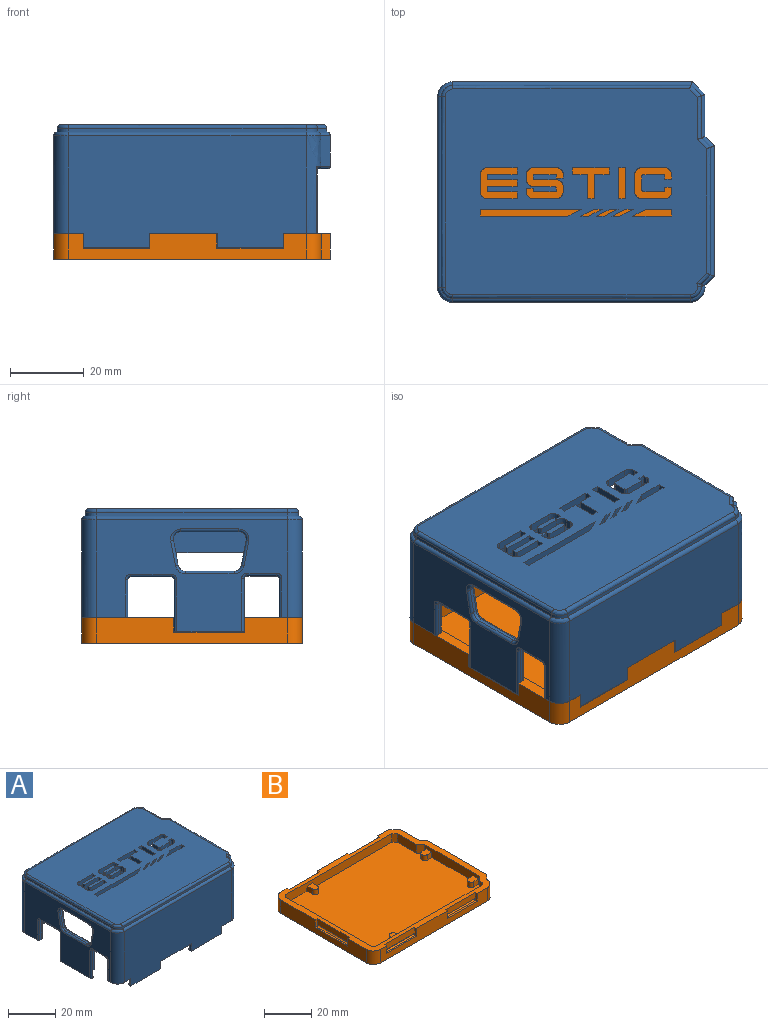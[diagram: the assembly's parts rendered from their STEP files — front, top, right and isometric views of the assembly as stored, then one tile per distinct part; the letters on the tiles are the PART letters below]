
ASSEMBLY  parts=2 mates=1
PART A: 255 faces, bbox 75.3x60.1x54.8 mm
  f0: plane 70.04x54.8mm, normal (0,0,-1), area 3493.9mm2, adj f16,f17,f18,f19,f20,f42,f43,f44
  f1: plane 71.33x56.09mm, normal (0,0,1), area 3615.8mm2, adj f61,f62,f63,f64,f65,f66,f67,f68
  f2: plane 19.01x1.65mm, normal (0,0,-1), area 31.1mm2, adj f43,f74,f79,f99,f129,f150
  f3: plane 17.92x0.8mm, normal (0,0,-1), area 14.3mm2, adj f39,f90,f98,f109
  f4: plane 17.92x0.8mm, normal (0,0,-1), area 14.3mm2, adj f41,f93,f96,f107
  f5: plane 17.92x3.15mm, normal (0,1,0), area 56.4mm2, adj f8,f90,f98,f110
  f6: plane 17.92x3.15mm, normal (0,-1,0), area 56.4mm2, adj f7,f93,f96,f108
  f7: plane 70.52x12.5mm, normal (0,0,-1), area 166.2mm2, adj f6,f10,f36,f37,f40,f41,f43,f44
  f8: plane 71.46x6.25mm, normal (0,0,-1), area 147.3mm2, adj f5,f9,f10,f11,f35,f38,f39,f42
  f9: plane 17.92x3.15mm, normal (0,1,0), area 56.4mm2, adj f8,f89,f97,f103
  f10: plane 51.81x30.35mm, normal (-1,0,0), area 907.2mm2, adj f7,f8,f25,f37,f38,f100,f119,f120
  f11: bspline ~27.5x4.44mm, area 110mm2, adj f8,f12,f28,f39,f156,f158
  f12: plane 8.25x2.54mm, normal (0.71,-0.71,0), area 29.6mm2, adj f11,f13,f29,f157
  f13: plane 35.43x8.25mm, normal (1,0,0), area 292.3mm2, adj f12,f14,f30,f155
  f14: plane 8.25x2.54mm, normal (0.71,0.71,0), area 29.6mm2, adj f13,f15,f31,f154
  f15: plane 11.43x8.25mm, normal (1,0,0), area 94.3mm2, adj f14,f32,f40,f153
  f16: plane 9.5x1.96mm, normal (-0.71,-0.71,0), area 26.4mm2, adj f0,f17,f44,f73
  f17: plane 11.43x9.5mm, normal (-1,0,0), area 108.5mm2, adj f0,f16,f18,f73
  f18: plane 9.5x2.54mm, normal (-0.71,-0.71,0), area 34.1mm2, adj f0,f17,f19,f73
  f19: plane 33.35x9.5mm, normal (-1,0,0), area 316.9mm2, adj f0,f18,f20,f73
  f20: plane 9.5x2.54mm, normal (-0.71,0.71,0), area 34.1mm2, adj f0,f19,f21,f59,f73
  f21: bspline ~50x2.98mm, area 29.3mm2, adj f20,f42,f59,f73
  f22: bspline ~2.41x1.59mm, area 0mm2, adj f24,f25,f53
  f23: bspline ~1.07x0.98mm, area 0.4mm2, adj f28,f29,f45
  f24: bspline ~4.08x4.06mm, area 8.8mm2, adj f22,f34,f37,f52
  f25: cylinder r=1mm len=51.81mm, axis (0,-1,0), area 81.4mm2, adj f10,f22,f26,f54
  f26: bspline ~4.05x4mm, area 8.8mm2, adj f25,f27,f38,f55
  f27: cylinder r=1mm len=64.54mm, axis (1,0,0), area 101.4mm2, adj f26,f28,f39,f56
  f28: bspline ~4.44x4.03mm, area 9.5mm2, adj f11,f23,f27,f29,f57
  f29: cylinder r=1mm len=3.61mm, axis (0.71,0.71,0), area 5.7mm2, adj f12,f23,f28,f30,f46
  f30: cylinder r=1mm len=35.43mm, axis (0,1,0), area 55mm2, adj f13,f29,f31,f47
  f31: cylinder r=1mm len=3.54mm, axis (-0.71,0.71,0), area 5.6mm2, adj f14,f30,f32,f48
  f32: cylinder r=1mm len=11.84mm, axis (0,1,0), area 17.9mm2, adj f15,f31,f33,f49
  f33: cylinder r=1mm len=4.13mm, axis (-0.71,0.71,0), area 7mm2, adj f32,f34,f40,f50
  f34: cylinder r=1mm len=65.09mm, axis (-1,0,0), area 102mm2, adj f24,f33,f41,f51
  f35: bspline ~50x1.68mm, area 65.6mm2, adj f8,f42,f43,f60
  f36: bspline ~50x1.72mm, area 66mm2, adj f7,f43,f44,f58
  f37: bspline ~27.5x4.02mm, area 163.9mm2, adj f7,f10,f24,f41
  f38: bspline ~27.5x3.98mm, area 163.3mm2, adj f8,f10,f26,f39
  f39: plane 64.54x30.35mm, normal (0,-1,0), area 1848.4mm2, adj f3,f8,f11,f27,f38,f88,f89,f90
  f40: plane 26.5x3.43mm, normal (0.71,0.71,0), area 71.5mm2, adj f7,f15,f33,f41,f151,f152
  f41: plane 65.09x30.35mm, normal (0,1,0), area 1862.9mm2, adj f4,f7,f34,f37,f40,f92,f93,f94
  f42: plane 66.52x27mm, normal (0,1,0), area 1773.4mm2, adj f0,f8,f21,f35,f59,f60,f73,f156
  f43: plane 51.41x27mm, normal (1,0,0), area 855mm2, adj f0,f2,f7,f8,f35,f36,f58,f60
  f44: plane 65.58x27mm, normal (0,-1,0), area 1754.1mm2, adj f0,f7,f16,f36,f58,f73,f151
  f45: extruded ~1x0.43mm, area 0.4mm2, adj f23,f46,f57,f68
  f46: plane 2.61x2.61mm, normal (0.71,-0.71,0), area 3.7mm2, adj f29,f45,f47,f67
  f47: plane 34.6x1mm, normal (1,0,0), area 34.6mm2, adj f30,f46,f48,f65
  f48: plane 2.54x2.54mm, normal (0.71,0.71,0), area 3.6mm2, adj f31,f47,f49,f63
  f49: plane 11.43x1mm, normal (1,0,0), area 11.4mm2, adj f32,f48,f50,f61
  f50: plane 2.84x2.84mm, normal (0.71,0.71,0), area 4mm2, adj f33,f49,f51,f62
  f51: plane 64.64x1mm, normal (0,1,0), area 64.6mm2, adj f34,f50,f52,f64
  f52: extruded ~3.02x3.01mm, area 4.7mm2, adj f24,f51,f53,f66
  f53: plane 1x0mm, normal (-1,0,0), area 0mm2, adj f22,f52,f54
  f54: plane 51.79x1mm, normal (-1,0,0), area 51.8mm2, adj f25,f53,f55,f69
  f55: extruded ~2.99x2.99mm, area 4.6mm2, adj f26,f54,f56,f71
  f56: plane 64.51x1mm, normal (0,-1,0), area 64.5mm2, adj f27,f55,f57,f72
  f57: extruded ~3.35x3.01mm, area 5mm2, adj f28,f45,f56,f70
  f58: extruded ~2x1.71mm, area 5.3mm2, adj f0,f36,f43,f44
  f59: extruded ~2.98x2mm, area 7.8mm2, adj f0,f20,f21,f42
  f60: extruded ~2x1.68mm, area 5.3mm2, adj f0,f35,f42,f43
  f61: bspline ~12.63x1mm, area 18.5mm2, adj f1,f49,f62,f63
  f62: bspline ~3.55x3.55mm, area 5.9mm2, adj f1,f50,f61,f64
  f63: bspline ~3.82x3.82mm, area 5.8mm2, adj f1,f48,f61,f65
  f64: bspline ~67.87x1mm, area 104.5mm2, adj f1,f51,f62,f66
  f65: bspline ~38.06x1mm, area 55.5mm2, adj f1,f47,f63,f67
  f66: bspline ~3.11x3.03mm, area 6.8mm2, adj f1,f52,f64,f69
  f67: bspline ~3.72x3.72mm, area 6.1mm2, adj f1,f46,f65,f68
  f68: bspline ~1.19x1.08mm, area 1.1mm2, adj f1,f45,f67,f70
  f69: bspline ~51.79x1mm, area 84mm2, adj f1,f54,f66,f71
  f70: bspline ~3.35x3.14mm, area 7.2mm2, adj f1,f57,f68,f72
  f71: bspline ~3.02x3.02mm, area 6.6mm2, adj f1,f55,f69,f72
  f72: bspline ~64.51x1mm, area 104.7mm2, adj f1,f56,f70,f71
  f73: plane 55.28x6.34mm, normal (0,0,-1), area 101.2mm2, adj f16,f17,f18,f19,f20,f21,f42,f44
  f74: plane 14.1x1mm, normal (0,1,0), area 10.9mm2, adj f2,f99,f100,f101,f102,f144,f148,f150
  f75: plane 11.05x1mm, normal (0,0,-1), area 11.1mm2, adj f142,f143,f147,f148
  f76: plane 10.25x1mm, normal (0,-1,0), area 10.3mm2, adj f7,f139,f141,f142
  f77: plane 10.5x1mm, normal (0,1,0), area 10.5mm2, adj f8,f132,f136,f138
  f78: plane 8x1mm, normal (0,0,-1), area 8mm2, adj f130,f131,f135,f136
  f79: plane 14.35x1mm, normal (0,-1,0), area 11.2mm2, adj f2,f99,f100,f101,f102,f127,f129,f130
  f80: plane 6.7x1.29mm, normal (0,0.98,0.19), area 6.8mm2, adj f81,f85,f118,f126
  f81: cylinder r=2mm len=2.38mm, axis (-1,0,0), area 3.5mm2, adj f80,f82,f116,f125
  f82: plane 15.77x1mm, normal (0,0,-1), area 15.8mm2, adj f81,f83,f114,f123
  f83: cylinder r=2mm len=2.38mm, axis (-1,0,0), area 3.5mm2, adj f82,f84,f112,f121
  f84: plane 6.7x1.29mm, normal (0,-0.98,0.19), area 6.8mm2, adj f83,f86,f111,f119
  f85: cylinder r=2mm len=1.96mm, axis (-1,0,0), area 2.8mm2, adj f80,f87,f117,f124
  f86: cylinder r=2mm len=1.96mm, axis (-1,0,0), area 2.8mm2, adj f84,f87,f113,f120
  f87: plane 13.19x1mm, normal (0,0,1), area 13.2mm2, adj f85,f86,f115,f122
  f88: plane 17.92x0.8mm, normal (0,0,-1), area 14.3mm2, adj f39,f89,f97,f104
  f89: plane 3.85x1.49mm, normal (1,0,0), area 4.1mm2, adj f8,f9,f39,f88,f103,f104
  f90: plane 3.85x1.49mm, normal (-1,0,0), area 4.1mm2, adj f3,f5,f8,f39,f109,f110
  f91: plane 17.92x3.15mm, normal (0,-1,0), area 56.4mm2, adj f7,f94,f95,f105
  f92: plane 17.92x0.8mm, normal (0,0,-1), area 14.3mm2, adj f41,f94,f95,f106
  f93: plane 3.85x1.48mm, normal (-1,0,0), area 3.6mm2, adj f4,f6,f7,f41,f107,f108
  f94: plane 3.85x1.49mm, normal (1,0,0), area 3.6mm2, adj f7,f41,f91,f92,f105,f106
  f95: plane 3.85x1.48mm, normal (-1,0,0), area 3.6mm2, adj f7,f41,f91,f92,f105,f106
  f96: plane 3.85x1.48mm, normal (1,0,0), area 3.6mm2, adj f4,f6,f7,f41,f107,f108
  f97: plane 3.85x1.49mm, normal (-1,0,0), area 4.1mm2, adj f8,f9,f39,f88,f103,f104
  f98: plane 3.85x1.49mm, normal (1,0,0), area 4.1mm2, adj f3,f5,f8,f39,f109,f110
  f99: plane 19.01x3.15mm, normal (1,0,0), area 59.9mm2, adj f2,f74,f79,f101
  f100: plane 19.01x0.8mm, normal (0,0,-1), area 15mm2, adj f10,f74,f79,f102,f127,f144
  f101: bspline ~20.91x0.7mm, area 13.8mm2, adj f74,f79,f99,f102
  f102: bspline ~20.91x0.7mm, area 14.7mm2, adj f74,f79,f100,f101
  f103: bspline ~19.71x0.67mm, area 10.4mm2, adj f9,f89,f97,f104
  f104: bspline ~19.71x0.7mm, area 13.9mm2, adj f88,f89,f97,f103
  f105: bspline ~19.71x0.7mm, area 13mm2, adj f91,f94,f95,f106
  f106: bspline ~19.71x0.7mm, area 13.9mm2, adj f92,f94,f95,f105
  f107: bspline ~19.71x0.7mm, area 13.9mm2, adj f4,f93,f96,f108
  f108: bspline ~19.71x0.7mm, area 13mm2, adj f6,f93,f96,f107
  f109: bspline ~19.71x0.7mm, area 13.9mm2, adj f3,f90,f98,f110
  f110: bspline ~19.71x0.67mm, area 10.4mm2, adj f5,f90,f98,f109
  f111: cylinder r=0.75mm len=6.84mm, axis (0,0.19,0.98), area 8mm2, adj f43,f84,f112,f113
  f112: torus R=2.75mm, axis (-1,0,0), area 4.7mm2, adj f43,f83,f111,f114
  f113: torus R=2.75mm, axis (-1,0,0), area 3.7mm2, adj f43,f86,f111,f115
  f114: cylinder r=0.75mm len=15.77mm, axis (0,-1,0), area 18.6mm2, adj f43,f82,f112,f116
  f115: cylinder r=0.75mm len=13.19mm, axis (0,1,0), area 15.5mm2, adj f43,f87,f113,f117
  f116: torus R=2.75mm, axis (-1,0,0), area 4.7mm2, adj f43,f81,f114,f118
  f117: torus R=2.75mm, axis (-1,0,0), area 3.7mm2, adj f43,f85,f115,f118
  f118: cylinder r=0.75mm len=6.84mm, axis (0,0.19,-0.98), area 8mm2, adj f43,f80,f116,f117
  f119: cylinder r=0.75mm len=6.84mm, axis (0,0.19,0.98), area 8mm2, adj f10,f84,f120,f121
  f120: torus R=2.75mm, axis (-1,0,0), area 3.7mm2, adj f10,f86,f119,f122
  f121: torus R=2.75mm, axis (-1,0,0), area 4.7mm2, adj f10,f83,f119,f123
  f122: cylinder r=0.75mm len=13.19mm, axis (0,1,0), area 15.5mm2, adj f10,f87,f120,f124
  f123: cylinder r=0.75mm len=15.77mm, axis (0,-1,0), area 18.6mm2, adj f10,f82,f121,f125
  f124: torus R=2.75mm, axis (-1,0,0), area 3.7mm2, adj f10,f85,f122,f126
  f125: torus R=2.75mm, axis (-1,0,0), area 4.7mm2, adj f10,f81,f123,f126
  f126: cylinder r=0.75mm len=6.84mm, axis (0,0.19,-0.98), area 8mm2, adj f10,f80,f124,f125
  f127: cylinder r=0.75mm len=14.35mm, axis (0,0,1), area 16.9mm2, adj f10,f79,f100,f128
  f128: torus R=1.5mm, axis (-1,0,0), area 1.9mm2, adj f10,f127,f130,f131
  f129: cylinder r=0.75mm len=10.5mm, axis (0,0,1), area 12.4mm2, adj f2,f43,f79,f133
  f130: cylinder r=0.75mm len=1mm, axis (1,0,0), area 1.2mm2, adj f78,f79,f128,f133
  f131: cylinder r=0.75mm len=8mm, axis (0,-1,0), area 9.4mm2, adj f10,f78,f128,f134
  f132: cylinder r=0.75mm len=10.5mm, axis (0,0,-1), area 12.4mm2, adj f8,f10,f77,f134
  f133: torus R=1.5mm, axis (-1,0,0), area 1.9mm2, adj f43,f129,f130,f135
  f134: torus R=1.5mm, axis (-1,0,0), area 1.9mm2, adj f10,f131,f132,f136
  f135: cylinder r=0.75mm len=8mm, axis (0,-1,0), area 9.4mm2, adj f43,f78,f133,f137
  f136: cylinder r=0.75mm len=1mm, axis (1,0,0), area 1.2mm2, adj f77,f78,f134,f137
  f137: torus R=1.5mm, axis (-1,0,0), area 1.9mm2, adj f43,f135,f136,f138
  f138: cylinder r=0.75mm len=10.5mm, axis (0,0,-1), area 12.4mm2, adj f8,f43,f77,f137
  f139: cylinder r=0.75mm len=10.25mm, axis (0,0,1), area 12.1mm2, adj f7,f10,f76,f140
  f140: torus R=1.5mm, axis (-1,0,0), area 1.9mm2, adj f10,f139,f142,f143
  f141: cylinder r=0.75mm len=10.25mm, axis (0,0,1), area 12.1mm2, adj f7,f43,f76,f145
  f142: cylinder r=0.75mm len=1mm, axis (1,0,0), area 1.2mm2, adj f75,f76,f140,f145
  f143: cylinder r=0.75mm len=11.05mm, axis (0,-1,0), area 13mm2, adj f10,f75,f140,f146
  f144: cylinder r=0.75mm len=14.1mm, axis (0,0,-1), area 16.6mm2, adj f10,f74,f100,f146
  f145: torus R=1.5mm, axis (-1,0,0), area 1.9mm2, adj f43,f141,f142,f147
  f146: torus R=1.5mm, axis (-1,0,0), area 1.9mm2, adj f10,f143,f144,f148
  f147: cylinder r=0.75mm len=11.05mm, axis (0,-1,0), area 13mm2, adj f43,f75,f145,f149
  f148: cylinder r=0.75mm len=1mm, axis (1,0,0), area 1.2mm2, adj f74,f75,f146,f149
  f149: torus R=1.5mm, axis (-1,0,0), area 1.9mm2, adj f43,f147,f148,f150
  f150: cylinder r=0.75mm len=10.25mm, axis (0,0,-1), area 12.1mm2, adj f2,f43,f74,f149
  f151: cylinder r=0.75mm len=18.25mm, axis (0,0,-1), area 31.4mm2, adj f7,f40,f44,f73,f152
  f152: cylinder r=0.75mm len=2.74mm, axis (-0.71,0.71,0), area 3.1mm2, adj f40,f73,f151,f153
  f153: cylinder r=0.75mm len=11.74mm, axis (0,1,0), area 13.5mm2, adj f15,f73,f152,f154
  f154: cylinder r=0.75mm len=3.29mm, axis (-0.71,0.71,0), area 4.2mm2, adj f14,f73,f153,f155
  f155: cylinder r=0.75mm len=35.43mm, axis (0,1,0), area 41.4mm2, adj f13,f73,f154,f157
  f156: cylinder r=0.75mm len=18.25mm, axis (0,0,1), area 31.6mm2, adj f8,f11,f42,f73,f158
  f157: cylinder r=0.75mm len=3.32mm, axis (0.71,0.71,0), area 4.3mm2, adj f12,f73,f155,f158
  f158: bspline ~4.3x2.3mm, area 3.7mm2, adj f11,f73,f156,f157
  f159: plane 8.13x2.5mm, normal (0,-1,0), area 20.3mm2, adj f0,f1,f160,f174
  f160: extruded ~2.5x1.88mm, area 7.4mm2, adj f0,f1,f159,f161
  f161: plane 4.69x2.5mm, normal (1,0,0), area 11.7mm2, adj f0,f1,f160,f162
  f162: extruded ~2.5x1.88mm, area 7.4mm2, adj f0,f1,f161,f163
  f163: plane 8.13x2.5mm, normal (0,1,0), area 20.3mm2, adj f0,f1,f162,f164
  f164: plane 2.5x1.88mm, normal (-1,0,0), area 4.7mm2, adj f0,f1,f163,f165
  f165: plane 7.81x2.5mm, normal (0,-1,0), area 19.5mm2, adj f0,f1,f164,f166
  f166: extruded ~2.5x0.31mm, area 1.2mm2, adj f0,f1,f165,f167
  f167: plane 2.5x1.09mm, normal (-1,0,0), area 2.7mm2, adj f0,f1,f166,f168
  f168: plane 8.13x2.5mm, normal (0,1,0), area 20.3mm2, adj f0,f1,f167,f169
  f169: plane 2.5x1.88mm, normal (-1,0,0), area 4.7mm2, adj f0,f1,f168,f170
  f170: plane 8.13x2.5mm, normal (0,-1,0), area 20.3mm2, adj f0,f1,f169,f171
  f171: plane 2.5x1.09mm, normal (-1,0,0), area 2.7mm2, adj f0,f1,f170,f172
  f172: extruded ~2.5x0.31mm, area 1.2mm2, adj f0,f1,f171,f173
  f173: plane 7.81x2.5mm, normal (0,1,0), area 19.5mm2, adj f0,f1,f172,f174
  f174: plane 2.5x1.88mm, normal (-1,0,0), area 4.7mm2, adj f0,f1,f159,f173
  f175: plane 6.8x2.5mm, normal (0,-1,0), area 17mm2, adj f0,f1,f176,f178
  f176: plane 3.75x2.5mm, normal (0.45,-0.89,0), area 10.5mm2, adj f0,f1,f175,f177
  f177: plane 10.55x2.5mm, normal (0,1,0), area 26.4mm2, adj f0,f1,f176,f178
  f178: plane 2.5x1.88mm, normal (-1,0,0), area 4.7mm2, adj f0,f1,f175,f177
  f179: plane 2.5x2.13mm, normal (0,-1,0), area 5.3mm2, adj f0,f1,f180,f182
  f180: plane 3.75x2.5mm, normal (0.45,-0.89,0), area 10.5mm2, adj f0,f1,f179,f181
  f181: plane 2.5x2.13mm, normal (0,1,0), area 5.3mm2, adj f0,f1,f180,f182
  f182: plane 3.75x2.5mm, normal (-0.45,0.89,0), area 10.5mm2, adj f0,f1,f179,f181
  f183: plane 27.51x2.5mm, normal (0,-1,0), area 68.8mm2, adj f0,f1,f184,f186
  f184: plane 2.5x1.88mm, normal (1,0,0), area 4.7mm2, adj f0,f1,f183,f185
  f185: plane 23.76x2.5mm, normal (0,1,0), area 59.4mm2, adj f0,f1,f184,f186
  f186: plane 3.75x2.5mm, normal (-0.45,0.89,0), area 10.5mm2, adj f0,f1,f183,f185
  f187: plane 2.5x2.13mm, normal (0,-1,0), area 5.3mm2, adj f0,f1,f188,f190
  f188: plane 3.75x2.5mm, normal (0.45,-0.89,0), area 10.5mm2, adj f0,f1,f187,f189
  f189: plane 2.5x2.13mm, normal (0,1,0), area 5.3mm2, adj f0,f1,f188,f190
  f190: plane 3.75x2.5mm, normal (-0.45,0.89,0), area 10.5mm2, adj f0,f1,f187,f189
  f191: plane 2.5x2.13mm, normal (0,-1,0), area 5.3mm2, adj f0,f1,f192,f194
  f192: plane 3.75x2.5mm, normal (0.45,-0.89,0), area 10.5mm2, adj f0,f1,f191,f193
  f193: plane 2.5x2.13mm, normal (0,1,0), area 5.3mm2, adj f0,f1,f192,f194
  f194: plane 3.75x2.5mm, normal (-0.45,0.89,0), area 10.5mm2, adj f0,f1,f191,f193
  f195: extruded ~2.5x0.63mm, area 2.5mm2, adj f0,f1,f196,f214
  f196: plane 5.31x2.5mm, normal (0,1,0), area 13.3mm2, adj f0,f1,f195,f197
  f197: extruded ~2.5x0.31mm, area 1.2mm2, adj f0,f1,f196,f198
  f198: plane 2.5x0.94mm, normal (1,0,0), area 2.3mm2, adj f0,f1,f197,f199
  f199: plane 2.5x1.88mm, normal (0,1,0), area 4.7mm2, adj f0,f1,f198,f200
  f200: plane 2.5x1.25mm, normal (-1,0,0), area 3.1mm2, adj f0,f1,f199,f201
  f201: extruded ~2.5x1.88mm, area 7.4mm2, adj f0,f1,f200,f202
  f202: plane 6.25x2.5mm, normal (0,-1,0), area 15.6mm2, adj f0,f1,f201,f203
  f203: extruded ~2.5x1.88mm, area 7.4mm2, adj f0,f1,f202,f204
  f204: plane 4.69x2.5mm, normal (1,0,0), area 11.7mm2, adj f0,f1,f203,f205
  f205: extruded ~2.5x1.88mm, area 7.4mm2, adj f0,f1,f204,f206
  f206: plane 6.25x2.5mm, normal (0,1,0), area 15.6mm2, adj f0,f1,f205,f207
  f207: extruded ~2.5x1.88mm, area 7.4mm2, adj f0,f1,f206,f208
  f208: plane 2.5x1.25mm, normal (-1,0,0), area 3.1mm2, adj f0,f1,f207,f209
  f209: plane 2.5x1.88mm, normal (0,-1,0), area 4.7mm2, adj f0,f1,f208,f210
  f210: plane 2.5x0.94mm, normal (1,0,0), area 2.3mm2, adj f0,f1,f209,f211
  f211: extruded ~2.5x0.31mm, area 1.2mm2, adj f0,f1,f210,f212
  f212: plane 5.31x2.5mm, normal (0,-1,0), area 13.3mm2, adj f0,f1,f211,f213
  f213: extruded ~2.5x0.63mm, area 2.5mm2, adj f0,f1,f212,f214
  f214: plane 3.44x2.5mm, normal (-1,0,0), area 8.6mm2, adj f0,f1,f195,f213
  f215: plane 8.44x2.5mm, normal (1,0,0), area 21.1mm2, adj f0,f1,f216,f218
  f216: plane 2.5x1.88mm, normal (0,1,0), area 4.7mm2, adj f0,f1,f215,f217
  f217: plane 8.44x2.5mm, normal (-1,0,0), area 21.1mm2, adj f0,f1,f216,f218
  f218: plane 2.5x1.88mm, normal (0,-1,0), area 4.7mm2, adj f0,f1,f215,f217
  f219: plane 6.56x2.5mm, normal (-1,0,0), area 16.4mm2, adj f0,f1,f220,f226
  f220: plane 4.06x2.5mm, normal (0,1,0), area 10.2mm2, adj f0,f1,f219,f221
  f221: plane 2.5x1.88mm, normal (-1,0,0), area 4.7mm2, adj f0,f1,f220,f222
  f222: plane 10x2.5mm, normal (0,-1,0), area 25mm2, adj f0,f1,f221,f223
  f223: plane 2.5x1.88mm, normal (1,0,0), area 4.7mm2, adj f0,f1,f222,f224
  f224: plane 4.06x2.5mm, normal (0,1,0), area 10.2mm2, adj f0,f1,f223,f225
  f225: plane 6.56x2.5mm, normal (1,0,0), area 16.4mm2, adj f0,f1,f224,f226
  f226: plane 2.5x1.88mm, normal (0,1,0), area 4.7mm2, adj f0,f1,f219,f225
  f227: extruded ~2.5x1.88mm, area 7.4mm2, adj f0,f1,f228,f254
  f228: plane 2.5x1.41mm, normal (1,0,0), area 3.5mm2, adj f0,f1,f227,f229
  f229: extruded ~2.5x1.88mm, area 7.4mm2, adj f0,f1,f228,f230
  f230: plane 5.94x2.5mm, normal (0,1,0), area 14.8mm2, adj f0,f1,f229,f231
  f231: extruded ~2.5x0.31mm, area 1.2mm2, adj f0,f1,f230,f232
  f232: plane 2.5x0.78mm, normal (1,0,0), area 2mm2, adj f0,f1,f231,f233
  f233: extruded ~2.5x0.31mm, area 1.2mm2, adj f0,f1,f232,f234
  f234: plane 5.63x2.5mm, normal (0,-1,0), area 14.1mm2, adj f0,f1,f233,f235
  f235: extruded ~2.5x0.31mm, area 1.2mm2, adj f0,f1,f234,f236
  f236: plane 2.5x0.63mm, normal (-1,0,0), area 1.6mm2, adj f0,f1,f235,f237
  f237: plane 2.5x1.88mm, normal (0,-1,0), area 4.7mm2, adj f0,f1,f236,f238
  f238: plane 2.5x0.94mm, normal (1,0,0), area 2.3mm2, adj f0,f1,f237,f239
  f239: extruded ~2.5x1.88mm, area 7.4mm2, adj f0,f1,f238,f240
  f240: plane 6.25x2.5mm, normal (0,1,0), area 15.6mm2, adj f0,f1,f239,f241
  f241: extruded ~2.5x1.88mm, area 7.4mm2, adj f0,f1,f240,f242
  f242: plane 2.5x1.41mm, normal (-1,0,0), area 3.5mm2, adj f0,f1,f241,f243
  f243: extruded ~2.5x1.88mm, area 7.4mm2, adj f0,f1,f242,f244
  f244: plane 5.94x2.5mm, normal (0,-1,0), area 14.8mm2, adj f0,f1,f243,f245
  f245: extruded ~2.5x0.31mm, area 1.2mm2, adj f0,f1,f244,f246
  f246: plane 2.5x0.78mm, normal (-1,0,0), area 2mm2, adj f0,f1,f245,f247
  f247: extruded ~2.5x0.31mm, area 1.2mm2, adj f0,f1,f246,f248
  f248: plane 5.63x2.5mm, normal (0,1,0), area 14.1mm2, adj f0,f1,f247,f249
  f249: extruded ~2.5x0.31mm, area 1.2mm2, adj f0,f1,f248,f250
  f250: plane 2.5x0.63mm, normal (1,0,0), area 1.6mm2, adj f0,f1,f249,f251
  f251: plane 2.5x1.88mm, normal (0,1,0), area 4.7mm2, adj f0,f1,f250,f252
  f252: plane 2.5x0.94mm, normal (-1,0,0), area 2.3mm2, adj f0,f1,f251,f253
  f253: extruded ~2.5x1.88mm, area 7.4mm2, adj f0,f1,f252,f254
  f254: plane 6.25x2.5mm, normal (0,-1,0), area 15.6mm2, adj f0,f1,f227,f253
PART B: 84 faces, bbox 75.1x59.9x11.6 mm
  f0: plane 18.12x0.06mm, normal (0,-0.93,0.38), area 1.2mm2, adj f8,f10,f25,f29
  f1: plane 18.12x0.06mm, normal (0,-0.93,0.38), area 1.2mm2, adj f9,f11,f26,f28
  f2: plane 19.2x0.06mm, normal (-0.93,0,0.38), area 1.3mm2, adj f3,f12,f30,f32
  f3: plane 19.2x0.06mm, normal (-0.9,0,-0.43), area 1.3mm2, adj f2,f13,f30,f32
  f4: plane 18.12x0.06mm, normal (0,0.93,0.38), area 1.2mm2, adj f6,f18,f50,f52
  f5: plane 18.12x0.06mm, normal (0,0.93,0.38), area 1.2mm2, adj f7,f19,f53,f55
  f6: plane 18.12x0.06mm, normal (0,0.9,-0.43), area 1.2mm2, adj f4,f20,f50,f52
  f7: plane 18.12x0.06mm, normal (0,0.9,-0.43), area 1.2mm2, adj f5,f21,f53,f55
  f8: plane 18.12x0.06mm, normal (0,-0.9,-0.43), area 1.2mm2, adj f0,f22,f25,f29
  f9: plane 18.12x0.06mm, normal (0,-0.9,-0.43), area 1.2mm2, adj f1,f23,f26,f28
  f10: bspline ~18.12x0.78mm, area 17.4mm2, adj f0,f24,f25,f29
  f11: bspline ~18.12x0.78mm, area 17.4mm2, adj f1,f26,f27,f28
  f12: bspline ~19.2x0.78mm, area 18.5mm2, adj f2,f30,f31,f32
  f13: bspline ~19.2x0.43mm, area 11.3mm2, adj f3,f30,f32,f33
  f14: cylinder r=1.61mm len=3.22mm, axis (0,0,-1), area 13.9mm2, adj f43,f44,f45,f48
  f15: cylinder r=1.61mm len=3.22mm, axis (0,0,-1), area 13.9mm2, adj f40,f41,f42,f48
  f16: cylinder r=1.61mm len=3.22mm, axis (0,0,-1), area 13.9mm2, adj f37,f38,f39,f48
  f17: cylinder r=1.61mm len=3.22mm, axis (0,0,-1), area 13.9mm2, adj f34,f35,f36,f48
  f18: bspline ~18.12x0.78mm, area 17.4mm2, adj f4,f50,f51,f52
  f19: bspline ~18.12x0.78mm, area 17.4mm2, adj f5,f53,f54,f55
  f20: bspline ~18.12x0.43mm, area 10.7mm2, adj f6,f50,f52,f58
  f21: bspline ~18.12x0.43mm, area 10.7mm2, adj f7,f53,f55,f59
  f22: bspline ~18.12x0.43mm, area 10.7mm2, adj f8,f25,f29,f64
  f23: bspline ~18.12x0.43mm, area 10.7mm2, adj f9,f26,f28,f65
  f24: plane 18.12x0.8mm, normal (0,0,1), area 14.5mm2, adj f10,f25,f29,f66
  f25: plane 4.01x1.61mm, normal (1,0,0), area 4.9mm2, adj f0,f8,f10,f22,f24,f64,f66,f82
  f26: plane 4.03x1.64mm, normal (-1,0,0), area 4.9mm2, adj f1,f9,f11,f23,f27,f65,f66,f82
  f27: plane 18.12x0.8mm, normal (0,0,1), area 14.5mm2, adj f11,f26,f28,f66
  f28: plane 4.01x1.61mm, normal (1,0,0), area 4.9mm2, adj f1,f9,f11,f23,f27,f65,f66,f82
  f29: plane 4.03x1.64mm, normal (-1,0,0), area 4.9mm2, adj f0,f8,f10,f22,f24,f64,f66,f82
  f30: plane 4.03x1.64mm, normal (0,1,0), area 4.9mm2, adj f2,f3,f12,f13,f31,f33,f68,f69
  f31: plane 19.2x0.8mm, normal (0,0,1), area 15.3mm2, adj f12,f30,f32,f68
  f32: plane 4.01x1.61mm, normal (0,-1,0), area 4.9mm2, adj f2,f3,f12,f13,f31,f33,f56,f68
  f33: plane 19.2x3.04mm, normal (-1,0,0), area 58.5mm2, adj f13,f30,f32,f70
  f34: plane 2.75x2.51mm, normal (1,0,0), area 6.9mm2, adj f17,f36,f48,f71
  f35: plane 2.75x2.51mm, normal (-1,0,0), area 6.9mm2, adj f17,f36,f48,f71
  f36: plane 4.11x3.22mm, normal (0,0,1), area 12.1mm2, adj f17,f34,f35,f71
  f37: plane 2.79x2.75mm, normal (0,-1,0), area 7.7mm2, adj f16,f38,f48,f74
  f38: plane 4.4x3.22mm, normal (0,0,1), area 13mm2, adj f16,f37,f39,f74
  f39: plane 2.79x2.75mm, normal (0,1,0), area 7.7mm2, adj f16,f38,f48,f74
  f40: plane 2.79x2.75mm, normal (0,-1,0), area 7.7mm2, adj f15,f41,f48,f74
  f41: plane 4.4x3.22mm, normal (0,0,1), area 13mm2, adj f15,f40,f42,f74
  f42: plane 2.79x2.75mm, normal (0,1,0), area 7.7mm2, adj f15,f41,f48,f74
  f43: plane 3.07x2.75mm, normal (1,0,0), area 8.4mm2, adj f14,f44,f48,f77
  f44: plane 4.68x3.22mm, normal (0,0,1), area 13.9mm2, adj f14,f43,f45,f77
  f45: plane 3.07x2.75mm, normal (-1,0,0), area 8.4mm2, adj f14,f44,f48,f77
  f46: plane 4.5x1.67mm, normal (-0.71,-0.71,0), area 10.6mm2, adj f48,f76,f77,f82
  f47: bspline ~9x1.26mm, area 8.7mm2, adj f48,f77,f78,f82
  f48: plane 69.12x53.88mm, normal (0,0,1), area 3612.9mm2, adj f14,f15,f16,f17,f34,f35,f37,f39
  f49: bspline ~9x1.23mm, area 8.6mm2, adj f48,f71,f78,f82
  f50: plane 4.03x1.64mm, normal (1,0,0), area 4.9mm2, adj f4,f6,f18,f20,f51,f58,f79,f82
  f51: plane 18.12x0.8mm, normal (0,0,1), area 14.5mm2, adj f18,f50,f52,f79
  f52: plane 4.01x1.61mm, normal (-1,0,0), area 4.9mm2, adj f4,f6,f18,f20,f51,f58,f79,f82
  f53: plane 4.03x1.64mm, normal (1,0,0), area 4.9mm2, adj f5,f7,f19,f21,f54,f59,f79,f82
  f54: plane 18.12x0.8mm, normal (0,0,1), area 14.5mm2, adj f19,f53,f55,f79
  f55: plane 4.01x1.61mm, normal (-1,0,0), area 4.9mm2, adj f5,f7,f19,f21,f54,f59,f79,f82
  f56: plane 1.15x0mm, normal (0,-1,0), area 0mm2, adj f32,f68,f70,f82
  f57: bspline ~7x4.02mm, area 43.3mm2, adj f68,f79,f80,f82
  f58: plane 18.12x3.04mm, normal (0,1,0), area 55.2mm2, adj f20,f50,f52,f82
  f59: plane 18.12x3.04mm, normal (0,1,0), area 55.2mm2, adj f21,f53,f55,f82
  f60: plane 7x2.54mm, normal (0.71,0.71,0), area 25.1mm2, adj f61,f80,f81,f82
  f61: plane 35.43x7mm, normal (1,0,0), area 248mm2, adj f60,f62,f80,f82
  f62: plane 7x2.54mm, normal (0.71,-0.71,0), area 25.1mm2, adj f61,f63,f80,f82
  f63: bspline ~7x4.44mm, area 46.3mm2, adj f62,f66,f80,f82
  f64: plane 18.12x3.04mm, normal (0,-1,0), area 55.2mm2, adj f22,f25,f29,f82
  f65: plane 18.12x3.04mm, normal (0,-1,0), area 55.2mm2, adj f23,f26,f28,f82
  f66: plane 64.54x7mm, normal (0,-1,0), area 306.9mm2, adj f24,f25,f26,f27,f28,f29,f63,f67
  f67: bspline ~7x3.98mm, area 43.1mm2, adj f66,f68,f80,f82
  f68: plane 51.81x7mm, normal (-1,0,0), area 285.8mm2, adj f30,f31,f32,f56,f57,f67,f69,f80
  f69: plane 1.15x0mm, normal (0,1,0), area 0mm2, adj f30,f68,f70,f82
  f70: plane 19.2x0mm, normal (-1,0,0), area 0mm2, adj f33,f56,f69,f82
  f71: plane 64.05x4.5mm, normal (0,1,0), area 279.4mm2, adj f34,f35,f36,f48,f49,f72,f82
  f72: bspline ~9x2.69mm, area 15.1mm2, adj f48,f71,f73,f82
  f73: plane 4.5x2.54mm, normal (-0.71,0.71,0), area 16.2mm2, adj f48,f72,f74,f82
  f74: plane 32.94x4.5mm, normal (-1,0,0), area 130.5mm2, adj f37,f38,f39,f40,f41,f42,f48,f73
  f75: plane 4.5x2.54mm, normal (-0.71,-0.71,0), area 16.2mm2, adj f48,f74,f76,f82
  f76: plane 11.43x4.5mm, normal (-1,0,0), area 51.4mm2, adj f46,f48,f75,f82
  f77: plane 63.6x4.5mm, normal (0,-1,0), area 277.4mm2, adj f43,f44,f45,f46,f47,f48,f82
  f78: plane 51.33x4.5mm, normal (1,0,0), area 231mm2, adj f47,f48,f49,f82
  f79: plane 65.09x7mm, normal (0,1,0), area 310.7mm2, adj f50,f51,f52,f53,f54,f55,f57,f80
  f80: plane 75.04x59.81mm, normal (0,0,-1), area 4414.5mm2, adj f57,f60,f61,f62,f63,f66,f67,f68
  f81: plane 11.43x7mm, normal (1,0,0), area 80mm2, adj f60,f80,f82,f83
  f82: plane 75.09x59.85mm, normal (0,0,1), area 644mm2, adj f25,f26,f28,f29,f46,f47,f49,f50
  f83: plane 7x3.43mm, normal (0.71,0.71,0), area 33.9mm2, adj f79,f80,f81,f82
PLACE A at identity
PLACE B at identity fixed
MATE fastened B.f82 <-> A.f7  axis (0,0,1) through (35.16,59.8,7)mm
